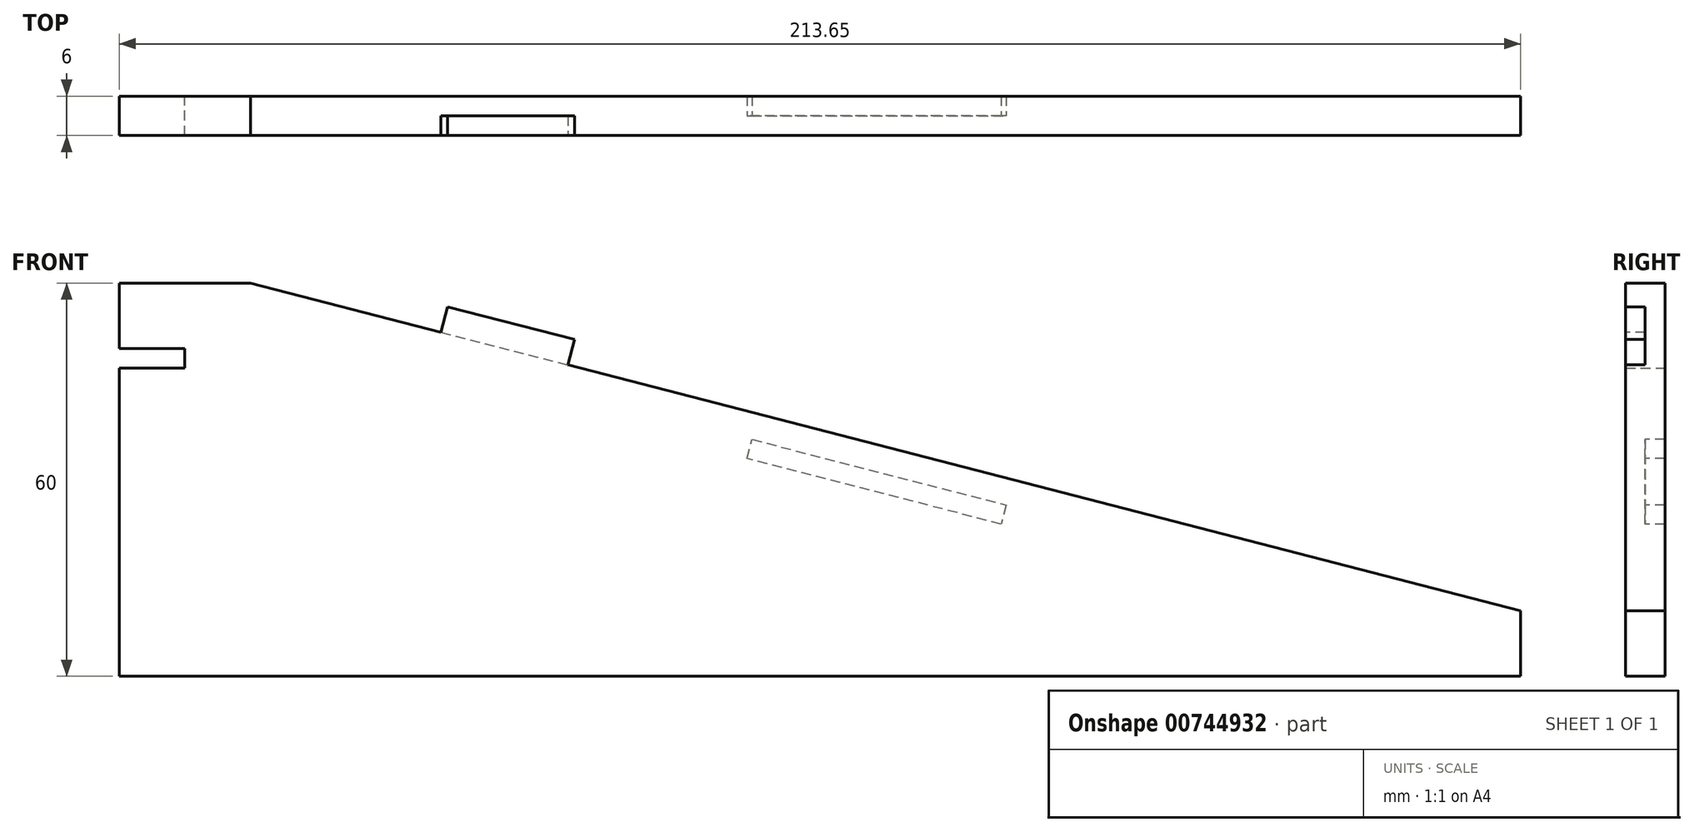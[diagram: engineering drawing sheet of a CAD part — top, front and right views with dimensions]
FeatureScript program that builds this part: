
annotation { "Feature Type Name" : "Feature", "Feature Type Description" : "" }
export const myFeature = defineFeature(function(context is Context, id is Id, definition is map)
    precondition{}
    {
        {
            var Q0;
            Q0=qCreatedBy(makeId("Front.planeOp"),FACE);
            var sketch = newSketch(context, id + "F0", { "sketchPlane" : qUnion([Q0])});
            skLineSegment(sketch, "E0", {"start": v(50, 0) * mm, "end": v(243.65, -50) * mm});
            skLineSegment(sketch, "E1", {"start": v(50, 0) * mm, "end": v(30, 0) * mm});
            skLineSegment(sketch, "E2", {"start": v(30, 0) * mm, "end": v(30, -10) * mm});
            skLineSegment(sketch, "E3", {"start": v(30, -10) * mm, "end": v(40, -10) * mm});
            skLineSegment(sketch, "E4", {"start": v(40, -10) * mm, "end": v(40, -13) * mm});
            skLineSegment(sketch, "E5", {"start": v(40, -13) * mm, "end": v(30, -13) * mm});
            skLineSegment(sketch, "E6", {"start": v(30, -13) * mm, "end": v(30, -60) * mm});
            skLineSegment(sketch, "E7", {"start": v(126.46, -23.87) * mm, "end": v(165.19, -33.87) * mm});
            skLineSegment(sketch, "E8", {"start": v(165.19, -33.87) * mm, "end": v(164.44, -36.78) * mm});
            skLineSegment(sketch, "E9", {"start": v(164.44, -36.78) * mm, "end": v(125.7, -26.78) * mm});
            skLineSegment(sketch, "E10", {"start": v(125.7, -26.78) * mm, "end": v(126.46, -23.87) * mm});
            skLineSegment(sketch, "E11", {"start": v(145.82, -28.87) * mm, "end": v(146.82, -25) * mm});
            skLineSegment(sketch, "E12", {"start": v(30, -60) * mm, "end": v(243.65, -60) * mm});
            skLineSegment(sketch, "E13", {"start": v(243.65, -60) * mm, "end": v(243.65, -50) * mm});
            skSolve(sketch);
        }
        {
            var Q0;
            Q0 = qSketchRegion(id + "F0", true);
            extrude(context, id + "F1", {"entities" : qUnion([Q0]), "depth" : 3 * mm, "offsetDistance" : 25 * mm});
        }
        {
            var Q0;
            Q0=makeQuery(id+"F1.opExtrude","CAP_FACE",FACE,{"disambiguationData":[OSD([sQuery(id+"F0.wireOp",EDGE,"E0"),sQuery(id+"F0.wireOp",EDGE,"yT4vIsvJ-HWam-oUay-oAL0-RhugAkDMXc1w"),sQuery(id+"F0.wireOp",EDGE,"E1"),sQuery(id+"F0.wireOp",EDGE,"E2"),sQuery(id+"F0.wireOp",EDGE,"E3"),sQuery(id+"F0.wireOp",EDGE,"E4"),sQuery(id+"F0.wireOp",EDGE,"E5"),sQuery(id+"F0.wireOp",EDGE,"E6"),sQuery(id+"F0.wireOp",EDGE,"E7"),sQuery(id+"F0.wireOp",EDGE,"E8"),sQuery(id+"F0.wireOp",EDGE,"E9"),sQuery(id+"F0.wireOp",EDGE,"E10")])],"isStart":false});
            var sketch = newSketch(context, id + "F2", { "sketchPlane" : qUnion([Q0])});
            skLineSegment(sketch, "E14", {"start": v(79.05, -7.5) * mm, "end": v(80.05, -3.63) * mm});
            skLineSegment(sketch, "E15", {"start": v(80.05, -3.63) * mm, "end": v(99.41, -8.63) * mm});
            skLineSegment(sketch, "E16", {"start": v(99.41, -8.63) * mm, "end": v(98.41, -12.5) * mm});
            skLineSegment(sketch, "E17", {"start": v(98.41, -12.5) * mm, "end": v(79.05, -7.5) * mm});
            skLineSegment(sketch, "E18", {"start": v(195.24, -37.5) * mm, "end": v(196.24, -33.63) * mm});
            skLineSegment(sketch, "E19", {"start": v(196.24, -33.63) * mm, "end": v(215.6, -38.63) * mm});
            skLineSegment(sketch, "E20", {"start": v(215.6, -38.63) * mm, "end": v(214.6, -42.5) * mm});
            skLineSegment(sketch, "E21", {"start": v(214.6, -42.5) * mm, "end": v(195.24, -37.5) * mm});
            skSolve(sketch);
        }
        {
            var Q0;
            Q0=makeQuery(id+"F2.imprint","IMPRINT",FACE,{"disambiguationData":[TD([[makeQuery(id+"F2.imprint","IMPRINT",EDGE,{"derivedFrom":sQuery(id+"F2.wireOp",EDGE,"E14")}),-1.0]])]});
            var Q1;
            Q1=makeQuery(id+"F2.imprint","IMPRINT",FACE,{"disambiguationData":[TD([[makeQuery(id+"F2.imprint","IMPRINT",EDGE,{"derivedFrom":makeQuery(id+"F1.opExtrude","CAP_EDGE",EDGE,{"disambiguationData":[OSD([sQuery(id+"F0.wireOp",EDGE,"E7")])],"isStart":false})}),-1.0]])]});
            var Q2;
            {var subQ0=sQuery(id+"F2.wireOp",EDGE,"E17");Q2=makeQuery(id+"F2.imprint","IMPRINT",FACE,{"disambiguationData":[TD([[makeQuery(id+"F2.imprint","IMPRINT",EDGE,{"derivedFrom":subQ0}),-1.0]])]});}
            var Q3;
            Q3 = qSketchRegion(id + "F0", true);
            extrude(context, id + "F3", {"entities" : qUnion([Q0, Q1, Q2, Q3]), "operationType" : NewBodyOperationType.ADD, "oppositeDirection" : true, "depth" : 3 * mm, "offsetDistance" : 25 * mm});
        }
        {
            var Q0;
            Q0=qCreatedBy(makeId("Front.planeOp"),FACE);
            var sketch = newSketch(context, id + "F4", { "sketchPlane" : qUnion([Q0])});
            skLineSegment(sketch, "E22", {"start": v(50.17, 0) * mm, "end": v(250.17, 0) * mm});
            skLineSegment(sketch, "E23", {"start": v(250.17, 0) * mm, "end": v(244.02, -49.62) * mm});
            skSolve(sketch);
        }
    });
